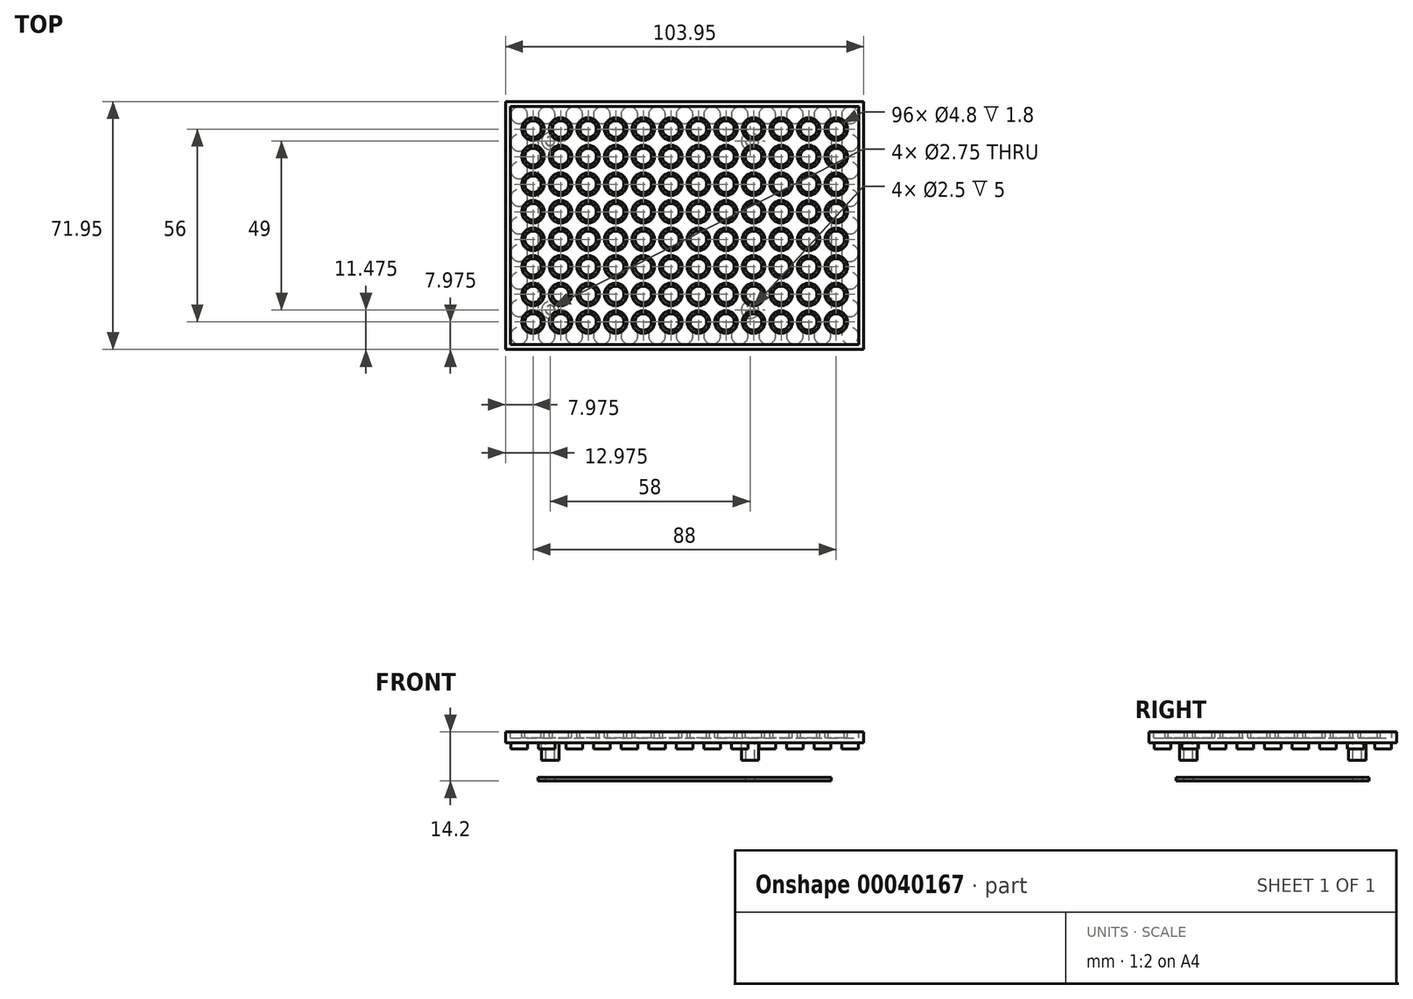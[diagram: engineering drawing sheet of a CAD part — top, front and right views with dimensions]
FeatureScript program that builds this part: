
annotation { "Feature Type Name" : "Feature", "Feature Type Description" : "" }
export const myFeature = defineFeature(function(context is Context, id is Id, definition is map)
    precondition{}
    {
        {
            var Q0;
            Q0=qCreatedBy(makeId("Top.planeOp"),FACE);
            var sketch = newSketch(context, id + "F0", { "sketchPlane" : qUnion([Q0])});
            skLineSegment(sketch, "E0.bottom", {"start": v(0, 0) * mm, "end": v(-103.95, 0) * mm});
            skLineSegment(sketch, "E0.top", {"start": v(0, 71.95) * mm, "end": v(-103.95, 71.95) * mm});
            skLineSegment(sketch, "E0.left", {"start": v(0, 0) * mm, "end": v(0, 71.95) * mm});
            skLineSegment(sketch, "E0.right", {"start": v(-103.95, 0) * mm, "end": v(-103.95, 71.95) * mm});
            skSolve(sketch);
        }
        {
            var Q0;
            Q0=makeQuery(id+"F0.imprint","IMPRINT",FACE,{"disambiguationData":[TD([[makeQuery(id+"F0.imprint","IMPRINT",EDGE,{"derivedFrom":sQuery(id+"F0.wireOp",EDGE,"E0.bottom")}),-1.0]])]});
            extrude(context, id + "F1", {"entities" : qUnion([Q0]), "oppositeDirection" : true, "depth" : 3.2 * mm});
        }
        {
            var Q0;
            Q0=qCreatedBy(makeId("Top.planeOp"),FACE);
            var sketch = newSketch(context, id + "F2", { "sketchPlane" : qUnion([Q0])});
            skLineSegment(sketch, "E1.bottom", {"start": v(-102.47, 1.47) * mm, "end": v(-1.47, 1.48) * mm});
            skLineSegment(sketch, "E1.top", {"start": v(-102.48, 70.47) * mm, "end": v(-1.48, 70.47) * mm});
            skLineSegment(sketch, "E1.left", {"start": v(-102.47, 1.47) * mm, "end": v(-102.48, 70.47) * mm});
            skLineSegment(sketch, "E1.right", {"start": v(-1.47, 1.48) * mm, "end": v(-1.48, 70.47) * mm});
            skCircle(sketch, "E2", {"center": v(-7.97, 7.98) * mm, "radius": 3.25 * mm});
            skCircle(sketch, "E3.0.1.0", {"center": v(-7.97, 15.98) * mm, "radius": 3.25 * mm});
            skCircle(sketch, "E3.0.2.0", {"center": v(-7.97, 23.98) * mm, "radius": 3.25 * mm});
            skCircle(sketch, "E3.0.3.0", {"center": v(-7.97, 31.98) * mm, "radius": 3.25 * mm});
            skCircle(sketch, "E3.0.4.0", {"center": v(-7.97, 39.98) * mm, "radius": 3.25 * mm});
            skCircle(sketch, "E3.0.5.0", {"center": v(-7.97, 47.98) * mm, "radius": 3.25 * mm});
            skCircle(sketch, "E3.0.6.0", {"center": v(-7.97, 55.98) * mm, "radius": 3.25 * mm});
            skCircle(sketch, "E3.0.7.0", {"center": v(-7.97, 63.98) * mm, "radius": 3.25 * mm});
            skCircle(sketch, "E3.1.0.0", {"center": v(-15.97, 7.98) * mm, "radius": 3.25 * mm});
            skCircle(sketch, "E3.1.1.0", {"center": v(-15.97, 15.98) * mm, "radius": 3.25 * mm});
            skCircle(sketch, "E3.1.2.0", {"center": v(-15.97, 23.98) * mm, "radius": 3.25 * mm});
            skCircle(sketch, "E3.1.3.0", {"center": v(-15.97, 31.98) * mm, "radius": 3.25 * mm});
            skCircle(sketch, "E3.1.4.0", {"center": v(-15.97, 39.98) * mm, "radius": 3.25 * mm});
            skCircle(sketch, "E3.1.5.0", {"center": v(-15.97, 47.98) * mm, "radius": 3.25 * mm});
            skCircle(sketch, "E3.1.6.0", {"center": v(-15.97, 55.98) * mm, "radius": 3.25 * mm});
            skCircle(sketch, "E3.1.7.0", {"center": v(-15.97, 63.98) * mm, "radius": 3.25 * mm});
            skCircle(sketch, "E3.2.0.0", {"center": v(-23.97, 7.98) * mm, "radius": 3.25 * mm});
            skCircle(sketch, "E3.2.1.0", {"center": v(-23.97, 15.98) * mm, "radius": 3.25 * mm});
            skCircle(sketch, "E3.2.2.0", {"center": v(-23.97, 23.98) * mm, "radius": 3.25 * mm});
            skCircle(sketch, "E3.2.3.0", {"center": v(-23.97, 31.98) * mm, "radius": 3.25 * mm});
            skCircle(sketch, "E3.2.4.0", {"center": v(-23.97, 39.98) * mm, "radius": 3.25 * mm});
            skCircle(sketch, "E3.2.5.0", {"center": v(-23.97, 47.98) * mm, "radius": 3.25 * mm});
            skCircle(sketch, "E3.2.6.0", {"center": v(-23.97, 55.98) * mm, "radius": 3.25 * mm});
            skCircle(sketch, "E3.2.7.0", {"center": v(-23.97, 63.98) * mm, "radius": 3.25 * mm});
            skCircle(sketch, "E3.3.0.0", {"center": v(-31.97, 7.98) * mm, "radius": 3.25 * mm});
            skCircle(sketch, "E3.3.1.0", {"center": v(-31.97, 15.98) * mm, "radius": 3.25 * mm});
            skCircle(sketch, "E3.3.2.0", {"center": v(-31.97, 23.98) * mm, "radius": 3.25 * mm});
            skCircle(sketch, "E3.3.3.0", {"center": v(-31.97, 31.98) * mm, "radius": 3.25 * mm});
            skCircle(sketch, "E3.3.4.0", {"center": v(-31.97, 39.98) * mm, "radius": 3.25 * mm});
            skCircle(sketch, "E3.3.5.0", {"center": v(-31.97, 47.98) * mm, "radius": 3.25 * mm});
            skCircle(sketch, "E3.3.6.0", {"center": v(-31.97, 55.98) * mm, "radius": 3.25 * mm});
            skCircle(sketch, "E3.3.7.0", {"center": v(-31.97, 63.98) * mm, "radius": 3.25 * mm});
            skCircle(sketch, "E3.4.0.0", {"center": v(-39.97, 7.98) * mm, "radius": 3.25 * mm});
            skCircle(sketch, "E3.4.1.0", {"center": v(-39.97, 15.98) * mm, "radius": 3.25 * mm});
            skCircle(sketch, "E3.4.2.0", {"center": v(-39.97, 23.98) * mm, "radius": 3.25 * mm});
            skCircle(sketch, "E3.4.3.0", {"center": v(-39.97, 31.98) * mm, "radius": 3.25 * mm});
            skCircle(sketch, "E3.4.4.0", {"center": v(-39.97, 39.98) * mm, "radius": 3.25 * mm});
            skCircle(sketch, "E3.4.5.0", {"center": v(-39.97, 47.98) * mm, "radius": 3.25 * mm});
            skCircle(sketch, "E3.4.6.0", {"center": v(-39.97, 55.98) * mm, "radius": 3.25 * mm});
            skCircle(sketch, "E3.4.7.0", {"center": v(-39.97, 63.98) * mm, "radius": 3.25 * mm});
            skCircle(sketch, "E3.5.0.0", {"center": v(-47.97, 7.98) * mm, "radius": 3.25 * mm});
            skCircle(sketch, "E3.5.1.0", {"center": v(-47.97, 15.98) * mm, "radius": 3.25 * mm});
            skCircle(sketch, "E3.5.2.0", {"center": v(-47.97, 23.98) * mm, "radius": 3.25 * mm});
            skCircle(sketch, "E3.5.3.0", {"center": v(-47.97, 31.98) * mm, "radius": 3.25 * mm});
            skCircle(sketch, "E3.5.4.0", {"center": v(-47.97, 39.98) * mm, "radius": 3.25 * mm});
            skCircle(sketch, "E3.5.5.0", {"center": v(-47.97, 47.98) * mm, "radius": 3.25 * mm});
            skCircle(sketch, "E3.5.6.0", {"center": v(-47.97, 55.98) * mm, "radius": 3.25 * mm});
            skCircle(sketch, "E3.5.7.0", {"center": v(-47.97, 63.98) * mm, "radius": 3.25 * mm});
            skCircle(sketch, "E3.6.0.0", {"center": v(-55.97, 7.98) * mm, "radius": 3.25 * mm});
            skCircle(sketch, "E3.6.1.0", {"center": v(-55.97, 15.98) * mm, "radius": 3.25 * mm});
            skCircle(sketch, "E3.6.2.0", {"center": v(-55.97, 23.98) * mm, "radius": 3.25 * mm});
            skCircle(sketch, "E3.6.3.0", {"center": v(-55.97, 31.98) * mm, "radius": 3.25 * mm});
            skCircle(sketch, "E3.6.4.0", {"center": v(-55.97, 39.98) * mm, "radius": 3.25 * mm});
            skCircle(sketch, "E3.6.5.0", {"center": v(-55.97, 47.98) * mm, "radius": 3.25 * mm});
            skCircle(sketch, "E3.6.6.0", {"center": v(-55.97, 55.98) * mm, "radius": 3.25 * mm});
            skCircle(sketch, "E3.6.7.0", {"center": v(-55.97, 63.98) * mm, "radius": 3.25 * mm});
            skCircle(sketch, "E3.7.0.0", {"center": v(-63.98, 7.98) * mm, "radius": 3.25 * mm});
            skCircle(sketch, "E3.7.1.0", {"center": v(-63.98, 15.98) * mm, "radius": 3.25 * mm});
            skCircle(sketch, "E3.7.2.0", {"center": v(-63.98, 23.98) * mm, "radius": 3.25 * mm});
            skCircle(sketch, "E3.7.3.0", {"center": v(-63.98, 31.98) * mm, "radius": 3.25 * mm});
            skCircle(sketch, "E3.7.4.0", {"center": v(-63.98, 39.98) * mm, "radius": 3.25 * mm});
            skCircle(sketch, "E3.7.5.0", {"center": v(-63.98, 47.98) * mm, "radius": 3.25 * mm});
            skCircle(sketch, "E3.7.6.0", {"center": v(-63.98, 55.98) * mm, "radius": 3.25 * mm});
            skCircle(sketch, "E3.7.7.0", {"center": v(-63.98, 63.98) * mm, "radius": 3.25 * mm});
            skCircle(sketch, "E3.8.0.0", {"center": v(-71.97, 7.98) * mm, "radius": 3.25 * mm});
            skCircle(sketch, "E3.8.1.0", {"center": v(-71.97, 15.98) * mm, "radius": 3.25 * mm});
            skCircle(sketch, "E3.8.2.0", {"center": v(-71.97, 23.98) * mm, "radius": 3.25 * mm});
            skCircle(sketch, "E3.8.3.0", {"center": v(-71.97, 31.98) * mm, "radius": 3.25 * mm});
            skCircle(sketch, "E3.8.4.0", {"center": v(-71.97, 39.98) * mm, "radius": 3.25 * mm});
            skCircle(sketch, "E3.8.5.0", {"center": v(-71.97, 47.98) * mm, "radius": 3.25 * mm});
            skCircle(sketch, "E3.8.6.0", {"center": v(-71.97, 55.98) * mm, "radius": 3.25 * mm});
            skCircle(sketch, "E3.8.7.0", {"center": v(-71.97, 63.98) * mm, "radius": 3.25 * mm});
            skCircle(sketch, "E3.9.0.0", {"center": v(-79.98, 7.98) * mm, "radius": 3.25 * mm});
            skCircle(sketch, "E3.9.1.0", {"center": v(-79.98, 15.98) * mm, "radius": 3.25 * mm});
            skCircle(sketch, "E3.9.2.0", {"center": v(-79.98, 23.98) * mm, "radius": 3.25 * mm});
            skCircle(sketch, "E3.9.3.0", {"center": v(-79.98, 31.98) * mm, "radius": 3.25 * mm});
            skCircle(sketch, "E3.9.4.0", {"center": v(-79.98, 39.98) * mm, "radius": 3.25 * mm});
            skCircle(sketch, "E3.9.5.0", {"center": v(-79.98, 47.98) * mm, "radius": 3.25 * mm});
            skCircle(sketch, "E3.9.6.0", {"center": v(-79.98, 55.98) * mm, "radius": 3.25 * mm});
            skCircle(sketch, "E3.9.7.0", {"center": v(-79.98, 63.98) * mm, "radius": 3.25 * mm});
            skCircle(sketch, "E3.10.0.0", {"center": v(-87.97, 7.98) * mm, "radius": 3.25 * mm});
            skCircle(sketch, "E3.10.1.0", {"center": v(-87.97, 15.98) * mm, "radius": 3.25 * mm});
            skCircle(sketch, "E3.10.2.0", {"center": v(-87.97, 23.98) * mm, "radius": 3.25 * mm});
            skCircle(sketch, "E3.10.3.0", {"center": v(-87.97, 31.98) * mm, "radius": 3.25 * mm});
            skCircle(sketch, "E3.10.4.0", {"center": v(-87.97, 39.98) * mm, "radius": 3.25 * mm});
            skCircle(sketch, "E3.10.5.0", {"center": v(-87.97, 47.98) * mm, "radius": 3.25 * mm});
            skCircle(sketch, "E3.10.6.0", {"center": v(-87.97, 55.98) * mm, "radius": 3.25 * mm});
            skCircle(sketch, "E3.10.7.0", {"center": v(-87.97, 63.98) * mm, "radius": 3.25 * mm});
            skCircle(sketch, "E3.11.0.0", {"center": v(-95.97, 7.98) * mm, "radius": 3.25 * mm});
            skCircle(sketch, "E3.11.1.0", {"center": v(-95.97, 15.98) * mm, "radius": 3.25 * mm});
            skCircle(sketch, "E3.11.2.0", {"center": v(-95.97, 23.98) * mm, "radius": 3.25 * mm});
            skCircle(sketch, "E3.11.3.0", {"center": v(-95.97, 31.98) * mm, "radius": 3.25 * mm});
            skCircle(sketch, "E3.11.4.0", {"center": v(-95.97, 39.98) * mm, "radius": 3.25 * mm});
            skCircle(sketch, "E3.11.5.0", {"center": v(-95.97, 47.98) * mm, "radius": 3.25 * mm});
            skCircle(sketch, "E3.11.6.0", {"center": v(-95.97, 55.98) * mm, "radius": 3.25 * mm});
            skCircle(sketch, "E3.11.7.0", {"center": v(-95.97, 63.98) * mm, "radius": 3.25 * mm});
            skLineSegment(sketch, "E3.direction1", {"start": v(-7.97, 7.98) * mm, "end": v(-15.97, 7.98) * mm, "construction": true});
            skLineSegment(sketch, "E3.direction2", {"start": v(-7.97, 7.98) * mm, "end": v(-7.97, 15.98) * mm, "construction": true});
            skSolve(sketch);
        }
        {
            var Q0;
            {var subQ0=sQuery(id+"F0.wireOp",EDGE,"E0.bottom");var subQ1=sQuery(id+"F0.wireOp",EDGE,"E0.top");var subQ2=sQuery(id+"F0.wireOp",EDGE,"E0.left");var subQ3=sQuery(id+"F0.wireOp",EDGE,"E0.right");Q0=makeQuery(id+"F4.boolean.opBoolean","SPLIT",FACE,{"disambiguationData":[TD([makeQuery(id+"F1.opExtrude","SWEPT_FACE",FACE,{"disambiguationData":[OSD([subQ0])]})])],"derivedFrom":makeQuery(id+"F1.opExtrude","CAP_FACE",FACE,{"disambiguationData":[OSD([subQ0,subQ1,subQ2,subQ3])],"isStart":true})});}
            var sketch = newSketch(context, id + "F3", { "sketchPlane" : qUnion([Q0])});
            skCircle(sketch, "E4", {"center": v(-7.98, 7.97) * mm, "radius": 2.4 * mm});
            skCircle(sketch, "E5.0.1.0", {"center": v(-7.98, 15.97) * mm, "radius": 2.4 * mm});
            skCircle(sketch, "E5.0.2.0", {"center": v(-7.98, 23.97) * mm, "radius": 2.4 * mm});
            skCircle(sketch, "E5.0.3.0", {"center": v(-7.98, 31.97) * mm, "radius": 2.4 * mm});
            skCircle(sketch, "E5.0.4.0", {"center": v(-7.98, 39.97) * mm, "radius": 2.4 * mm});
            skCircle(sketch, "E5.0.5.0", {"center": v(-7.98, 47.97) * mm, "radius": 2.4 * mm});
            skCircle(sketch, "E5.0.6.0", {"center": v(-7.98, 55.97) * mm, "radius": 2.4 * mm});
            skCircle(sketch, "E5.0.7.0", {"center": v(-7.98, 63.97) * mm, "radius": 2.4 * mm});
            skCircle(sketch, "E5.1.0.0", {"center": v(-15.98, 7.97) * mm, "radius": 2.4 * mm});
            skCircle(sketch, "E5.1.1.0", {"center": v(-15.98, 15.97) * mm, "radius": 2.4 * mm});
            skCircle(sketch, "E5.1.2.0", {"center": v(-15.98, 23.97) * mm, "radius": 2.4 * mm});
            skCircle(sketch, "E5.1.3.0", {"center": v(-15.98, 31.97) * mm, "radius": 2.4 * mm});
            skCircle(sketch, "E5.1.4.0", {"center": v(-15.98, 39.97) * mm, "radius": 2.4 * mm});
            skCircle(sketch, "E5.1.5.0", {"center": v(-15.98, 47.97) * mm, "radius": 2.4 * mm});
            skCircle(sketch, "E5.1.6.0", {"center": v(-15.98, 55.97) * mm, "radius": 2.4 * mm});
            skCircle(sketch, "E5.1.7.0", {"center": v(-15.98, 63.97) * mm, "radius": 2.4 * mm});
            skCircle(sketch, "E5.2.0.0", {"center": v(-23.98, 7.97) * mm, "radius": 2.4 * mm});
            skCircle(sketch, "E5.2.1.0", {"center": v(-23.98, 15.97) * mm, "radius": 2.4 * mm});
            skCircle(sketch, "E5.2.2.0", {"center": v(-23.98, 23.97) * mm, "radius": 2.4 * mm});
            skCircle(sketch, "E5.2.3.0", {"center": v(-23.98, 31.97) * mm, "radius": 2.4 * mm});
            skCircle(sketch, "E5.2.4.0", {"center": v(-23.98, 39.97) * mm, "radius": 2.4 * mm});
            skCircle(sketch, "E5.2.5.0", {"center": v(-23.98, 47.97) * mm, "radius": 2.4 * mm});
            skCircle(sketch, "E5.2.6.0", {"center": v(-23.98, 55.97) * mm, "radius": 2.4 * mm});
            skCircle(sketch, "E5.2.7.0", {"center": v(-23.98, 63.97) * mm, "radius": 2.4 * mm});
            skCircle(sketch, "E5.3.0.0", {"center": v(-31.98, 7.97) * mm, "radius": 2.4 * mm});
            skCircle(sketch, "E5.3.1.0", {"center": v(-31.98, 15.97) * mm, "radius": 2.4 * mm});
            skCircle(sketch, "E5.3.2.0", {"center": v(-31.98, 23.97) * mm, "radius": 2.4 * mm});
            skCircle(sketch, "E5.3.3.0", {"center": v(-31.98, 31.97) * mm, "radius": 2.4 * mm});
            skCircle(sketch, "E5.3.4.0", {"center": v(-31.98, 39.97) * mm, "radius": 2.4 * mm});
            skCircle(sketch, "E5.3.5.0", {"center": v(-31.98, 47.97) * mm, "radius": 2.4 * mm});
            skCircle(sketch, "E5.3.6.0", {"center": v(-31.98, 55.97) * mm, "radius": 2.4 * mm});
            skCircle(sketch, "E5.3.7.0", {"center": v(-31.98, 63.97) * mm, "radius": 2.4 * mm});
            skCircle(sketch, "E5.4.0.0", {"center": v(-39.98, 7.97) * mm, "radius": 2.4 * mm});
            skCircle(sketch, "E5.4.1.0", {"center": v(-39.98, 15.97) * mm, "radius": 2.4 * mm});
            skCircle(sketch, "E5.4.2.0", {"center": v(-39.98, 23.97) * mm, "radius": 2.4 * mm});
            skCircle(sketch, "E5.4.3.0", {"center": v(-39.98, 31.97) * mm, "radius": 2.4 * mm});
            skCircle(sketch, "E5.4.4.0", {"center": v(-39.98, 39.97) * mm, "radius": 2.4 * mm});
            skCircle(sketch, "E5.4.5.0", {"center": v(-39.98, 47.97) * mm, "radius": 2.4 * mm});
            skCircle(sketch, "E5.4.6.0", {"center": v(-39.98, 55.97) * mm, "radius": 2.4 * mm});
            skCircle(sketch, "E5.4.7.0", {"center": v(-39.98, 63.97) * mm, "radius": 2.4 * mm});
            skCircle(sketch, "E5.5.0.0", {"center": v(-47.98, 7.97) * mm, "radius": 2.4 * mm});
            skCircle(sketch, "E5.5.1.0", {"center": v(-47.98, 15.97) * mm, "radius": 2.4 * mm});
            skCircle(sketch, "E5.5.2.0", {"center": v(-47.98, 23.97) * mm, "radius": 2.4 * mm});
            skCircle(sketch, "E5.5.3.0", {"center": v(-47.98, 31.97) * mm, "radius": 2.4 * mm});
            skCircle(sketch, "E5.5.4.0", {"center": v(-47.98, 39.97) * mm, "radius": 2.4 * mm});
            skCircle(sketch, "E5.5.5.0", {"center": v(-47.98, 47.97) * mm, "radius": 2.4 * mm});
            skCircle(sketch, "E5.5.6.0", {"center": v(-47.98, 55.97) * mm, "radius": 2.4 * mm});
            skCircle(sketch, "E5.5.7.0", {"center": v(-47.98, 63.97) * mm, "radius": 2.4 * mm});
            skCircle(sketch, "E5.6.0.0", {"center": v(-55.98, 7.97) * mm, "radius": 2.4 * mm});
            skCircle(sketch, "E5.6.1.0", {"center": v(-55.98, 15.97) * mm, "radius": 2.4 * mm});
            skCircle(sketch, "E5.6.2.0", {"center": v(-55.98, 23.97) * mm, "radius": 2.4 * mm});
            skCircle(sketch, "E5.6.3.0", {"center": v(-55.98, 31.97) * mm, "radius": 2.4 * mm});
            skCircle(sketch, "E5.6.4.0", {"center": v(-55.98, 39.97) * mm, "radius": 2.4 * mm});
            skCircle(sketch, "E5.6.5.0", {"center": v(-55.98, 47.97) * mm, "radius": 2.4 * mm});
            skCircle(sketch, "E5.6.6.0", {"center": v(-55.98, 55.97) * mm, "radius": 2.4 * mm});
            skCircle(sketch, "E5.6.7.0", {"center": v(-55.98, 63.97) * mm, "radius": 2.4 * mm});
            skCircle(sketch, "E5.7.0.0", {"center": v(-63.98, 7.97) * mm, "radius": 2.4 * mm});
            skCircle(sketch, "E5.7.1.0", {"center": v(-63.98, 15.97) * mm, "radius": 2.4 * mm});
            skCircle(sketch, "E5.7.2.0", {"center": v(-63.98, 23.97) * mm, "radius": 2.4 * mm});
            skCircle(sketch, "E5.7.3.0", {"center": v(-63.98, 31.97) * mm, "radius": 2.4 * mm});
            skCircle(sketch, "E5.7.4.0", {"center": v(-63.98, 39.97) * mm, "radius": 2.4 * mm});
            skCircle(sketch, "E5.7.5.0", {"center": v(-63.98, 47.97) * mm, "radius": 2.4 * mm});
            skCircle(sketch, "E5.7.6.0", {"center": v(-63.98, 55.97) * mm, "radius": 2.4 * mm});
            skCircle(sketch, "E5.7.7.0", {"center": v(-63.98, 63.97) * mm, "radius": 2.4 * mm});
            skCircle(sketch, "E5.8.0.0", {"center": v(-71.98, 7.97) * mm, "radius": 2.4 * mm});
            skCircle(sketch, "E5.8.1.0", {"center": v(-71.98, 15.97) * mm, "radius": 2.4 * mm});
            skCircle(sketch, "E5.8.2.0", {"center": v(-71.98, 23.97) * mm, "radius": 2.4 * mm});
            skCircle(sketch, "E5.8.3.0", {"center": v(-71.98, 31.97) * mm, "radius": 2.4 * mm});
            skCircle(sketch, "E5.8.4.0", {"center": v(-71.98, 39.97) * mm, "radius": 2.4 * mm});
            skCircle(sketch, "E5.8.5.0", {"center": v(-71.98, 47.97) * mm, "radius": 2.4 * mm});
            skCircle(sketch, "E5.8.6.0", {"center": v(-71.98, 55.97) * mm, "radius": 2.4 * mm});
            skCircle(sketch, "E5.8.7.0", {"center": v(-71.98, 63.97) * mm, "radius": 2.4 * mm});
            skCircle(sketch, "E5.9.0.0", {"center": v(-79.98, 7.97) * mm, "radius": 2.4 * mm});
            skCircle(sketch, "E5.9.1.0", {"center": v(-79.98, 15.97) * mm, "radius": 2.4 * mm});
            skCircle(sketch, "E5.9.2.0", {"center": v(-79.98, 23.97) * mm, "radius": 2.4 * mm});
            skCircle(sketch, "E5.9.3.0", {"center": v(-79.98, 31.97) * mm, "radius": 2.4 * mm});
            skCircle(sketch, "E5.9.4.0", {"center": v(-79.98, 39.97) * mm, "radius": 2.4 * mm});
            skCircle(sketch, "E5.9.5.0", {"center": v(-79.98, 47.97) * mm, "radius": 2.4 * mm});
            skCircle(sketch, "E5.9.6.0", {"center": v(-79.98, 55.97) * mm, "radius": 2.4 * mm});
            skCircle(sketch, "E5.9.7.0", {"center": v(-79.98, 63.97) * mm, "radius": 2.4 * mm});
            skCircle(sketch, "E5.10.0.0", {"center": v(-87.98, 7.97) * mm, "radius": 2.4 * mm});
            skCircle(sketch, "E5.10.1.0", {"center": v(-87.98, 15.97) * mm, "radius": 2.4 * mm});
            skCircle(sketch, "E5.10.2.0", {"center": v(-87.98, 23.97) * mm, "radius": 2.4 * mm});
            skCircle(sketch, "E5.10.3.0", {"center": v(-87.98, 31.97) * mm, "radius": 2.4 * mm});
            skCircle(sketch, "E5.10.4.0", {"center": v(-87.98, 39.97) * mm, "radius": 2.4 * mm});
            skCircle(sketch, "E5.10.5.0", {"center": v(-87.98, 47.97) * mm, "radius": 2.4 * mm});
            skCircle(sketch, "E5.10.6.0", {"center": v(-87.98, 55.97) * mm, "radius": 2.4 * mm});
            skCircle(sketch, "E5.10.7.0", {"center": v(-87.98, 63.97) * mm, "radius": 2.4 * mm});
            skCircle(sketch, "E5.11.0.0", {"center": v(-95.98, 7.97) * mm, "radius": 2.4 * mm});
            skCircle(sketch, "E5.11.1.0", {"center": v(-95.98, 15.97) * mm, "radius": 2.4 * mm});
            skCircle(sketch, "E5.11.2.0", {"center": v(-95.98, 23.97) * mm, "radius": 2.4 * mm});
            skCircle(sketch, "E5.11.3.0", {"center": v(-95.98, 31.97) * mm, "radius": 2.4 * mm});
            skCircle(sketch, "E5.11.4.0", {"center": v(-95.98, 39.97) * mm, "radius": 2.4 * mm});
            skCircle(sketch, "E5.11.5.0", {"center": v(-95.98, 47.97) * mm, "radius": 2.4 * mm});
            skCircle(sketch, "E5.11.6.0", {"center": v(-95.98, 55.97) * mm, "radius": 2.4 * mm});
            skCircle(sketch, "E5.11.7.0", {"center": v(-95.98, 63.97) * mm, "radius": 2.4 * mm});
            skLineSegment(sketch, "E5.direction1", {"start": v(-7.98, 7.97) * mm, "end": v(-15.98, 7.97) * mm, "construction": true});
            skLineSegment(sketch, "E5.direction2", {"start": v(-7.98, 7.97) * mm, "end": v(-7.98, 15.97) * mm, "construction": true});
            skSolve(sketch);
        }
        {
            var Q0;
            Q0=qSketchRegion(id+"F2",true);
            var Q1;
            Q1=qSketchRegion(id+"F3",true);
            var Q2;
            Q2=sQuery(id+"F2.wireOp",EDGE,"de4b574f-d5fe-483e-a269-1c24a673af37.0.MirrorC");
            extrude(context, id + "F4", {"entities" : qUnion([Q0, Q1]), "operationType" : NewBodyOperationType.REMOVE, "surfaceEntities" : qUnion([Q2]), "oppositeDirection" : true, "depth" : 1.8 * mm});
        }
        {
            var Q0;
            Q0=makeQuery(id+"F1.opExtrude","CAP_FACE",FACE,{"disambiguationData":[OSD([sQuery(id+"F0.wireOp",EDGE,"E0.bottom"),sQuery(id+"F0.wireOp",EDGE,"E0.top"),sQuery(id+"F0.wireOp",EDGE,"E0.left"),sQuery(id+"F0.wireOp",EDGE,"E0.right")])],"isStart":false});
            var sketch = newSketch(context, id + "F5", { "sketchPlane" : qUnion([Q0])});
            skCircle(sketch, "E6", {"center": v(-4, -4) * mm, "radius": 2.45 * mm});
            skCircle(sketch, "E7.0.1.0", {"center": v(-4, -68) * mm, "radius": 2.45 * mm});
            skCircle(sketch, "E7.1.0.0", {"center": v(-12, -4) * mm, "radius": 2.45 * mm});
            skCircle(sketch, "E7.1.1.0", {"center": v(-12, -68) * mm, "radius": 2.45 * mm});
            skCircle(sketch, "E7.2.0.0", {"center": v(-20, -4) * mm, "radius": 2.45 * mm});
            skCircle(sketch, "E7.2.1.0", {"center": v(-20, -68) * mm, "radius": 2.45 * mm});
            skCircle(sketch, "E7.3.0.0", {"center": v(-28, -4) * mm, "radius": 2.45 * mm});
            skCircle(sketch, "E7.3.1.0", {"center": v(-28, -68) * mm, "radius": 2.45 * mm});
            skCircle(sketch, "E7.4.0.0", {"center": v(-36, -4) * mm, "radius": 2.45 * mm});
            skCircle(sketch, "E7.4.1.0", {"center": v(-36, -68) * mm, "radius": 2.45 * mm});
            skCircle(sketch, "E7.5.0.0", {"center": v(-44, -4) * mm, "radius": 2.45 * mm});
            skCircle(sketch, "E7.5.1.0", {"center": v(-44, -68) * mm, "radius": 2.45 * mm});
            skCircle(sketch, "E7.6.0.0", {"center": v(-52, -4) * mm, "radius": 2.45 * mm});
            skCircle(sketch, "E7.6.1.0", {"center": v(-52, -68) * mm, "radius": 2.45 * mm});
            skCircle(sketch, "E7.7.0.0", {"center": v(-60, -4) * mm, "radius": 2.45 * mm});
            skCircle(sketch, "E7.7.1.0", {"center": v(-60, -68) * mm, "radius": 2.45 * mm});
            skCircle(sketch, "E7.8.0.0", {"center": v(-68, -4) * mm, "radius": 2.45 * mm});
            skCircle(sketch, "E7.8.1.0", {"center": v(-68, -68) * mm, "radius": 2.45 * mm});
            skCircle(sketch, "E7.9.0.0", {"center": v(-76, -4) * mm, "radius": 2.45 * mm});
            skCircle(sketch, "E7.9.1.0", {"center": v(-76, -68) * mm, "radius": 2.45 * mm});
            skCircle(sketch, "E7.10.0.0", {"center": v(-84, -4) * mm, "radius": 2.45 * mm});
            skCircle(sketch, "E7.10.1.0", {"center": v(-84, -68) * mm, "radius": 2.45 * mm});
            skCircle(sketch, "E7.11.0.0", {"center": v(-92, -4) * mm, "radius": 2.45 * mm});
            skCircle(sketch, "E7.11.1.0", {"center": v(-92, -68) * mm, "radius": 2.45 * mm});
            skCircle(sketch, "E7.12.0.0", {"center": v(-100, -4) * mm, "radius": 2.45 * mm});
            skCircle(sketch, "E7.12.1.0", {"center": v(-100, -68) * mm, "radius": 2.45 * mm});
            skLineSegment(sketch, "E7.direction1", {"start": v(-4, -4) * mm, "end": v(-12, -4) * mm, "construction": true});
            skLineSegment(sketch, "E7.direction2", {"start": v(-4, -4) * mm, "end": v(-4, -68) * mm, "construction": true});
            skCircle(sketch, "E8.0.1.0", {"center": v(-4, -12) * mm, "radius": 2.45 * mm});
            skCircle(sketch, "E8.0.2.0", {"center": v(-4, -20) * mm, "radius": 2.45 * mm});
            skCircle(sketch, "E8.0.3.0", {"center": v(-4, -28) * mm, "radius": 2.45 * mm});
            skCircle(sketch, "E8.0.4.0", {"center": v(-4, -36) * mm, "radius": 2.45 * mm});
            skCircle(sketch, "E8.0.5.0", {"center": v(-4, -44) * mm, "radius": 2.45 * mm});
            skCircle(sketch, "E8.0.6.0", {"center": v(-4, -52) * mm, "radius": 2.45 * mm});
            skCircle(sketch, "E8.0.7.0", {"center": v(-4, -60) * mm, "radius": 2.45 * mm});
            skLineSegment(sketch, "E8.direction1", {"start": v(-4, -4) * mm, "end": v(-46.45, -4) * mm, "construction": true});
            skLineSegment(sketch, "E8.direction2", {"start": v(-4, -4) * mm, "end": v(-4, -12) * mm, "construction": true});
            skCircle(sketch, "E9.0.1.0", {"center": v(-100, -12) * mm, "radius": 2.45 * mm});
            skCircle(sketch, "E9.0.2.0", {"center": v(-100, -20) * mm, "radius": 2.45 * mm});
            skCircle(sketch, "E9.0.3.0", {"center": v(-100, -28) * mm, "radius": 2.45 * mm});
            skCircle(sketch, "E9.0.4.0", {"center": v(-100, -36) * mm, "radius": 2.45 * mm});
            skCircle(sketch, "E9.0.5.0", {"center": v(-100, -44) * mm, "radius": 2.45 * mm});
            skCircle(sketch, "E9.0.6.0", {"center": v(-100, -52) * mm, "radius": 2.45 * mm});
            skCircle(sketch, "E9.0.7.0", {"center": v(-100, -60) * mm, "radius": 2.45 * mm});
            skLineSegment(sketch, "E9.direction1", {"start": v(-100, -4) * mm, "end": v(-75, -4) * mm, "construction": true});
            skLineSegment(sketch, "E9.direction2", {"start": v(-100, -4) * mm, "end": v(-100, -12) * mm, "construction": true});
            skSolve(sketch);
        }
        {
            var Q0;
            Q0=qSketchRegion(id+"F5",true);
            extrude(context, id + "F6", {"entities" : qUnion([Q0]), "operationType" : NewBodyOperationType.ADD, "depth" : 1.7 * mm});
        }
        {
            var Q0;
            Q0=makeQuery(id+"F1.opExtrude","CAP_FACE",FACE,{"disambiguationData":[OSD([sQuery(id+"F0.wireOp",EDGE,"E0.bottom"),sQuery(id+"F0.wireOp",EDGE,"E0.top"),sQuery(id+"F0.wireOp",EDGE,"E0.left"),sQuery(id+"F0.wireOp",EDGE,"E0.right")])],"isStart":false});
            var sketch = newSketch(context, id + "F7", { "sketchPlane" : qUnion([Q0])});
            skCircle(sketch, "E10", {"center": v(-32.97, -60.48) * mm, "radius": 1.25 * mm});
            skCircle(sketch, "E11", {"center": v(-32.97, -60.48) * mm, "radius": 2.5 * mm});
            skCircle(sketch, "E12", {"center": v(-90.97, -60.48) * mm, "radius": 1.25 * mm});
            skCircle(sketch, "E13", {"center": v(-90.97, -60.48) * mm, "radius": 2.5 * mm});
            skCircle(sketch, "E14", {"center": v(-32.98, -11.48) * mm, "radius": 1.25 * mm});
            skCircle(sketch, "E15", {"center": v(-32.98, -11.48) * mm, "radius": 2.5 * mm});
            skCircle(sketch, "E16", {"center": v(-90.97, -11.48) * mm, "radius": 1.25 * mm});
            skCircle(sketch, "E17", {"center": v(-90.97, -11.48) * mm, "radius": 2.5 * mm});
            skSolve(sketch);
        }
        {
            var Q0;
            Q0=qSketchRegion(id+"F7",true);
            extrude(context, id + "F8", {"entities" : qUnion([Q0]), "operationType" : NewBodyOperationType.ADD, "depth" : 5 * mm});
        }
        {
            var Q0;
            Q0=makeQuery(id+"F8.opExtrude","CAP_FACE",FACE,{"disambiguationData":[OSD([sQuery(id+"F7.wireOp",EDGE,"E10"),sQuery(id+"F7.wireOp",EDGE,"E11")])],"isStart":false});
            cPlane(context, id + "F9", {"entities" : qUnion([Q0]), "cplaneType" : CPlaneType.OFFSET, "offset" : 5 * mm, "width" : 150 * mm, "height" : 150 * mm});
        }
        {
            var Q0;
            Q0=qCreatedBy(id+"F9.planeOp",FACE);
            var sketch = newSketch(context, id + "F10", { "sketchPlane" : qUnion([Q0])});
            skLineSegment(sketch, "E18.bottom", {"start": v(-94.47, -63.98) * mm, "end": v(-9.47, -63.98) * mm});
            skLineSegment(sketch, "E18.top", {"start": v(-94.47, -7.98) * mm, "end": v(-9.47, -7.98) * mm});
            skLineSegment(sketch, "E18.left", {"start": v(-94.47, -63.98) * mm, "end": v(-94.47, -7.98) * mm});
            skLineSegment(sketch, "E18.right", {"start": v(-9.47, -63.98) * mm, "end": v(-9.47, -7.98) * mm});
            skSolve(sketch);
        }
        {
            var Q0;
            Q0=qSketchRegion(id+"F10",true);
            extrude(context, id + "F11", {"entities" : qUnion([Q0]), "depth" : 1 * mm});
        }
        {
            var Q0;
            Q0=makeQuery(id+"F11.opExtrude","SWEPT_EDGE",EDGE,{"disambiguationData":[OSD([sQuery(id+"F10.wireOp",EDGE,"E18.top"),sQuery(id+"F10.wireOp",EDGE,"E18.left")])]});
            var Q1;
            Q1=makeQuery(id+"F11.opExtrude","SWEPT_EDGE",EDGE,{"disambiguationData":[OSD([sQuery(id+"F10.wireOp",EDGE,"E18.bottom"),sQuery(id+"F10.wireOp",EDGE,"E18.left")])]});
            var Q2;
            Q2=makeQuery(id+"F11.opExtrude","SWEPT_EDGE",EDGE,{"disambiguationData":[OSD([sQuery(id+"F10.wireOp",EDGE,"E18.bottom"),sQuery(id+"F10.wireOp",EDGE,"E18.right")])]});
            var Q3;
            Q3=makeQuery(id+"F11.opExtrude","SWEPT_EDGE",EDGE,{"disambiguationData":[OSD([sQuery(id+"F10.wireOp",EDGE,"E18.top"),sQuery(id+"F10.wireOp",EDGE,"E18.right")])]});
            fillet(context, id + "F12", {"entities" : qUnion([Q0, Q1, Q2, Q3]), "radius" : 3 * mm, "allowEdgeOverflow" : false});
        }
        {
            var Q0;
            Q0=makeQuery(id+"F11.opExtrude","CAP_FACE",FACE,{"disambiguationData":[OSD([sQuery(id+"F10.wireOp",EDGE,"E18.bottom"),sQuery(id+"F10.wireOp",EDGE,"E18.top"),sQuery(id+"F10.wireOp",EDGE,"E18.left"),sQuery(id+"F10.wireOp",EDGE,"E18.right")])],"isStart":false});
            var sketch = newSketch(context, id + "F13", { "sketchPlane" : qUnion([Q0])});
            skCircle(sketch, "E19", {"center": v(-90.97, -60.48) * mm, "radius": 1.38 * mm});
            skCircle(sketch, "E20.0.1.0", {"center": v(-90.97, -11.47) * mm, "radius": 1.38 * mm});
            skCircle(sketch, "E20.1.0.0", {"center": v(-32.97, -60.47) * mm, "radius": 1.38 * mm});
            skCircle(sketch, "E20.1.1.0", {"center": v(-32.97, -11.47) * mm, "radius": 1.38 * mm});
            skLineSegment(sketch, "E20.direction1", {"start": v(-90.97, -60.48) * mm, "end": v(-32.97, -60.48) * mm, "construction": true});
            skLineSegment(sketch, "E20.direction2", {"start": v(-90.97, -60.48) * mm, "end": v(-90.97, -11.47) * mm, "construction": true});
            skSolve(sketch);
        }
        {
            var Q0;
            Q0=qSketchRegion(id+"F13",true);
            var Q1;
            Q1=makeQuery(id+"F11.opExtrude","CAP_FACE",FACE,{"disambiguationData":[OSD([sQuery(id+"F10.wireOp",EDGE,"E18.bottom"),sQuery(id+"F10.wireOp",EDGE,"E18.top"),sQuery(id+"F10.wireOp",EDGE,"E18.left"),sQuery(id+"F10.wireOp",EDGE,"E18.right")])],"isStart":true});
            extrude(context, id + "F14", {"entities" : qUnion([Q0]), "operationType" : NewBodyOperationType.REMOVE, "endBound" : BoundingType.UP_TO_SURFACE, "oppositeDirection" : true, "endBoundEntityFace" : qUnion([Q1]), "depth" : 25 * mm});
        }
    });
